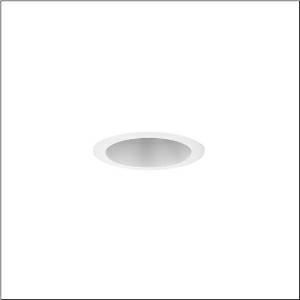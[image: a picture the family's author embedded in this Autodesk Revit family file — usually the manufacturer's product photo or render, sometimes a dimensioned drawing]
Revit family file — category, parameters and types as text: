
# Revit family: lunis_31-l_51dn15ee41b
name_source: partatom
category: Lighting Fixtures
units: mm (PartAtom-declared; Revit-internal decimal feet)

## family parameters
Cut with Voids When Loaded = No
Host = Face
Light Source = No
Part Type = Normal
Room Calculation Point = No
Round Connector Dimension = Use Diameter
Shared = No

## types (1)
- --- (1 x LED, 1750 lm, 12.2 W, 4000K)
    Apparent Load = 12 VA
    CIE Flux Codes = 93 98 100 100 100
    Color Rendering = 80
    Color Temperature = 4000K
    Default Elevation = 1800 mm
    Description = Lunis 31, -L, downlight, light control with reflector, light emission: direct distribution, LED rated luminous flux: 1.750lm, light colour: 840, mains connection: 220..240V, AC/DC, 0/50..60Hz, housing, of aluminium, white, protection rating (complete): IP20, protection rating (on room side): IP54, insulation class (complete): insulation class II (safety insulation), certification: CE, ENEC, packaging unit: 1 piece
    Height = 0 mm  [stored 0 ft]
    Lamp = 1 x LED
    Lamp Light Flux = 1750 lm
    Lamp Power = 12.2 W
    Lamp count = 1
    Length = 188 mm  [stored 0.616798 ft]
    Luminous efficacy = 143 lm/W
    Manufacturer = Siteco
    ModVariant = No
    Model = 51DN15EE41B
    Mounting Place = Ceiling
    Mounting Type = Recessed
    Number of Poles = 1
    OnlyDefault = Yes
    Power Factor = 1
    Product Name = Lunis 31-L
    Product group = downlight
    ProductGroupID = 401
    Protection Class = Protection class II
    Protection Degree = IP 20
    RLX_Detail_Level = 1
    RLX_Emergency_Light_Flux = 0 lm
    RLX_Emergency_Type = 0
    RLX_Emergency_Type_DB = No
    RlxData = <blob elided: 22229 chars, md5=caee145f>
    Socket = socket
    Standby Power = 0 W
    System Light Flux = 1750 lm
    System Power = 12 W
    Type Comments = individual setting: luminous flux: 100 % | (OFF | ON) | 300 mA
    Type Image = l_1345911.jpg
    URL = http://relux.com
    VarID = @adj_029747
    Voltage = 0 V
    Weight = 0.00 kg
    Width = 0 mm  [stored 0 ft]

note: [stored X ft] marks values corroborated as IEEE doubles in the binary element streams (Revit-internal decimal feet)

## geometry (parser evidence)
native form markers: Blend x4, Sweep x10
no freeform markers — native parametric forms only
